# Revit family: Shower-Valves_and_Controls-KOHLER-MasterShower-K-728-K
name_source: partatom
category: Pipe Accessories
revit_build: Autodesk Revit 2015 (Build: 20140606_1530(x64)
units: mm (PartAtom-declared; Revit-internal decimal feet)

## types (1)
- K-728-K
    ADA Compliant = No
    Assembly Code = D2010900
    Brass = Brass - Kohler - Satin
    Date Modified = 09/26/2017
    Default Elevation = 42"
    Description = MasterShower 3/4 inch 2 or 3-way transfer valve
    Flow Rate = 21 GPM
    HW Connection = Yes
    Height = 4 3/16"
    Inlet Connector = Inlet Connection
    Length = 3 5/8"
    Manufacturer = Kohler
    MasterFormat 1995 = 10820
    MasterFormat 2004 = 10.28.13
    Material = Forged dezincification-resistant brass body
    Model = K-728-K-NA
    Outlet Connector = Outlet Connection
    Plastic = Plastic - Kohler - Black
    Pressure = 45.00 psi
    Product Documentation Link = http://www.us.kohler.com
    Product Name = MasterShower
    Product Page URL = http://www.us.kohler.com
    Type = 0
    URL = http://www.us.kohler.com
    Waste Connection = No
    Width = 3 3/8"

## geometry (parser evidence)
native form markers: Blend x4, Sweep x3
no freeform markers — native parametric forms only
